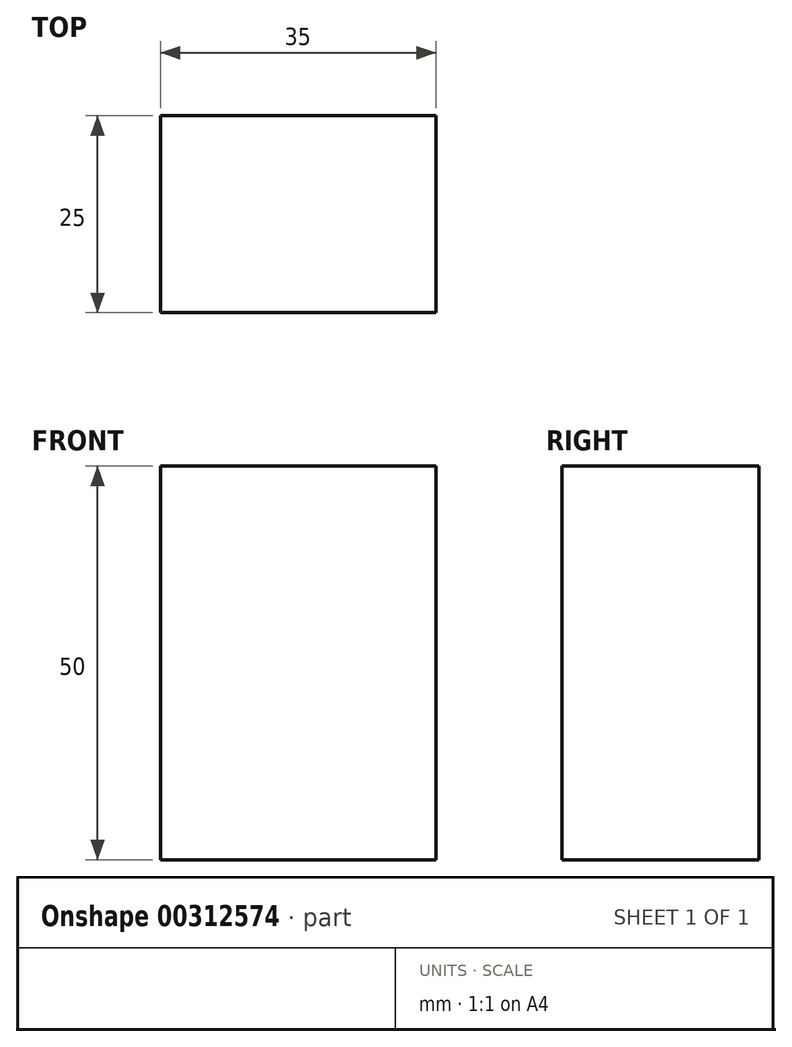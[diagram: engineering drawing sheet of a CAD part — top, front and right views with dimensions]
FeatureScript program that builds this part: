
annotation { "Feature Type Name" : "Feature", "Feature Type Description" : "" }
export const myFeature = defineFeature(function(context is Context, id is Id, definition is map)
    precondition{}
    {
        {
            var Q0;
            Q0=qCreatedBy(makeId("Front.planeOp"),FACE);
            var sketch = newSketch(context, id + "F0", { "sketchPlane" : qUnion([Q0])});
            skLineSegment(sketch, "E0.bottom", {"start": v(-17.5, 25) * mm, "end": v(17.5, 25) * mm});
            skLineSegment(sketch, "E0.top", {"start": v(-17.5, -25) * mm, "end": v(17.5, -25) * mm});
            skLineSegment(sketch, "E0.left", {"start": v(-17.5, 25) * mm, "end": v(-17.5, -25) * mm});
            skLineSegment(sketch, "E0.right", {"start": v(17.5, 25) * mm, "end": v(17.5, -25) * mm});
            skPoint(sketch, "E0.middle", {"position": v(0, 0) * mm});
            skLineSegment(sketch, "E1.bottom", {"start": v(0, 0) * mm, "end": v(35, 0) * mm});
            skLineSegment(sketch, "E1.top", {"start": v(0, -50) * mm, "end": v(35, -50) * mm});
            skLineSegment(sketch, "E1.left", {"start": v(0, 0) * mm, "end": v(0, -50) * mm});
            skLineSegment(sketch, "E1.right", {"start": v(35, 0) * mm, "end": v(35, -50) * mm});
            skSolve(sketch);
        }
        {
            var Q0;
            Q0 = qSketchRegion(id + "F0", true);
            var Q1;
            Q1=sQuery(id+"F0.wireOp",EDGE,"E0.bottom");
            var Q2;
            Q2=sQuery(id+"F0.wireOp",EDGE,"E0.left");
            var Q3;
            Q3=sQuery(id+"F0.wireOp",EDGE,"E0.right");
            var Q4;
            Q4=sQuery(id+"F0.wireOp",EDGE,"E0.top");
            extrude(context, id + "F1", {"entities" : qUnion([Q0]), "bodyType" : ToolBodyType.SURFACE, "operationType" : NewBodyOperationType.REMOVE, "surfaceEntities" : qUnion([Q1, Q2, Q3, Q4]), "oppositeDirection" : true, "depth" : 25 * mm});
        }
    });
